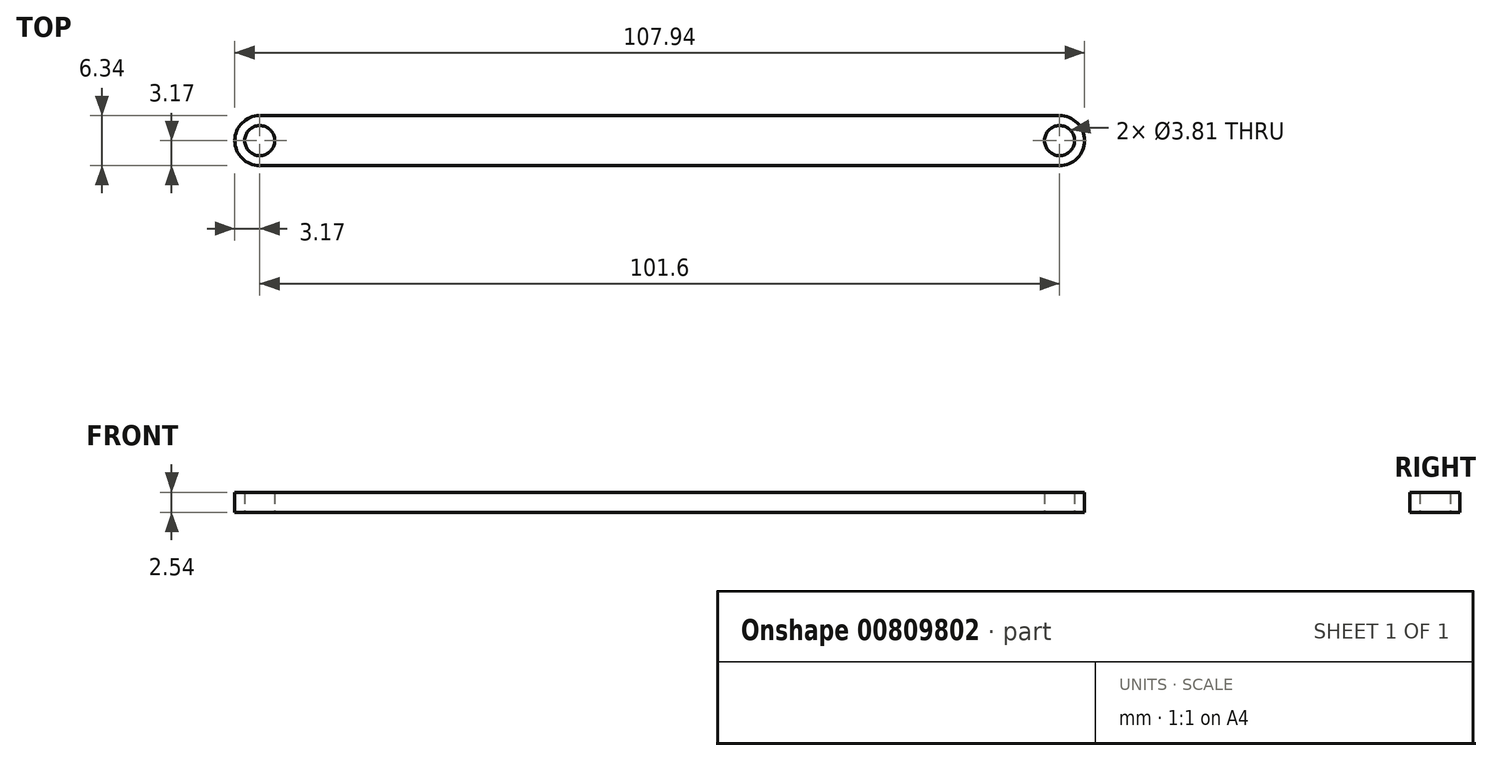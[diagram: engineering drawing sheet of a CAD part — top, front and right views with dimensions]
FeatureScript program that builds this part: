
annotation { "Feature Type Name" : "Feature", "Feature Type Description" : "" }
export const myFeature = defineFeature(function(context is Context, id is Id, definition is map)
    precondition{}
    {
        {
            var Q0;
            Q0=qCreatedBy(makeId("Top.planeOp"),FACE);
            var sketch = newSketch(context, id + "F0", { "sketchPlane" : qUnion([Q0])});
            skCircle(sketch, "E0", {"center": v(0, 0) * mm, "radius": 1.9 * mm});
            skCircle(sketch, "E1", {"center": v(0, 0) * mm, "radius": 3.18 * mm});
            skLineSegment(sketch, "E2", {"start": v(0, 3.18) * mm, "end": v(101.6, 3.18) * mm});
            skCircle(sketch, "E3", {"center": v(101.6, 0) * mm, "radius": 1.9 * mm});
            skCircle(sketch, "E4", {"center": v(101.6, 0) * mm, "radius": 3.17 * mm});
            skLineSegment(sketch, "E5", {"start": v(0, -3.17) * mm, "end": v(101.6, -3.17) * mm});
            skSolve(sketch);
        }
        {
            var Q0;
            Q0=qSketchRegion(id+"F0",true);
            extrude(context, id + "F1", {"entities" : qUnion([Q0]), "depth" : 2.54 * mm, "offsetDistance" : 25.4 * mm});
        }
    });
